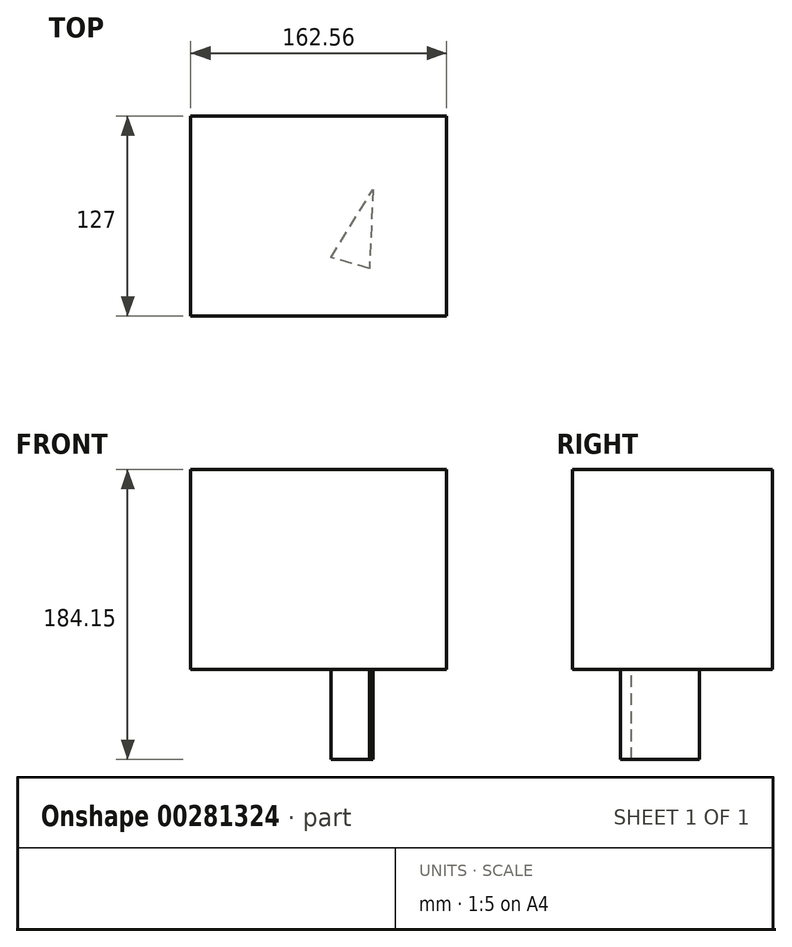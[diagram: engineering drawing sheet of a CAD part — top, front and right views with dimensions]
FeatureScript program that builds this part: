
annotation { "Feature Type Name" : "Feature", "Feature Type Description" : "" }
export const myFeature = defineFeature(function(context is Context, id is Id, definition is map)
    precondition{}
    {
        {
            var Q0;
            Q0=qCreatedBy(makeId("Front.planeOp"),FACE);
            var sketch = newSketch(context, id + "F0", { "sketchPlane" : qUnion([Q0])});
            skLineSegment(sketch, "E0.bottom", {"start": v(-127, 0) * mm, "end": v(0, 0) * mm});
            skLineSegment(sketch, "E0.top", {"start": v(-127, 127) * mm, "end": v(0, 127) * mm});
            skLineSegment(sketch, "E0.left", {"start": v(-127, 0) * mm, "end": v(-127, 127) * mm});
            skLineSegment(sketch, "E0.right", {"start": v(0, 0) * mm, "end": v(0, 127) * mm});
            skSolve(sketch);
        }
        {
            var Q0;
            Q0=qCreatedBy(makeId("Top.planeOp"),FACE);
            var sketch = newSketch(context, id + "F1", { "sketchPlane" : qUnion([Q0])});
            skLineSegment(sketch, "E1.bottom", {"start": v(0, 0) * mm, "end": v(0, 0) * mm});
            skLineSegment(sketch, "E1.top", {"start": v(0, -127) * mm, "end": v(0, -127) * mm});
            skLineSegment(sketch, "E1.left", {"start": v(0, 0) * mm, "end": v(0, -127) * mm});
            skLineSegment(sketch, "E1.right", {"start": v(0, 0) * mm, "end": v(0, -127) * mm});
            skLineSegment(sketch, "E2.left", {"start": v(0, -127) * mm, "end": v(0, 0) * mm});
            skLineSegment(sketch, "E2.right", {"start": v(0, -127) * mm, "end": v(0, 0) * mm});
            skLineSegment(sketch, "E3.bottom", {"start": v(0, -127) * mm, "end": v(-127, -127) * mm});
            skLineSegment(sketch, "E3.top", {"start": v(0, 0) * mm, "end": v(-127, 0) * mm});
            skLineSegment(sketch, "E3.right", {"start": v(-127, -127) * mm, "end": v(-127, 0) * mm});
            skSolve(sketch);
        }
        {
            var Q0;
            Q0=makeQuery(id+"F1.imprint","IMPRINT",FACE,{"disambiguationData":[TD([[makeQuery(id+"F1.imprint","IMPRINT",EDGE,{"derivedFrom":sQuery(id+"F1.wireOp",EDGE,"E3.bottom")}),-1.0]])]});
            extrude(context, id + "F2", {"entities" : qUnion([Q0]), "depth" : 127 * mm});
        }
        {
            var Q0;
            Q0=makeQuery(id+"F2.opExtrude","SWEPT_FACE",FACE,{"disambiguationData":[OSD([sQuery(id+"F1.wireOp",EDGE,"E3.right")])]});
            var sketch = newSketch(context, id + "F3", { "sketchPlane" : qUnion([Q0])});
            skSolve(sketch);
        }
        {
            var Q0;
            {var subQ0=sQuery(id+"F1.wireOp",EDGE,"E3.right");Q0=makeQuery(id+"F3.imprint","IMPRINT",FACE,{"disambiguationData":[TD([[makeQuery(id+"F3.imprint","IMPRINT",EDGE,{"derivedFrom":makeQuery(id+"F2.opExtrude","CAP_EDGE",EDGE,{"disambiguationData":[OSD([subQ0])],"isStart":true})}),-1.0]])]});}
            var sketch = newSketch(context, id + "F4", { "sketchPlane" : qUnion([Q0])});
            skCircle(sketch, "E4", {"center": v(63.3, 61.73) * mm, "radius": 31.75 * mm});
            skCircle(sketch, "E5", {"center": v(63.3, 61.73) * mm, "radius": 48.75 * mm});
            skSolve(sketch);
        }
        {
            var Q0;
            {var subQ0=sQuery(id+"F1.wireOp",EDGE,"E3.right");Q0=makeQuery(id+"F3.imprint","IMPRINT",FACE,{"disambiguationData":[TD([[makeQuery(id+"F3.imprint","IMPRINT",EDGE,{"derivedFrom":makeQuery(id+"F2.opExtrude","CAP_EDGE",EDGE,{"disambiguationData":[OSD([subQ0])],"isStart":true})}),-1.0]])]});}
            var sketch = newSketch(context, id + "F5", { "sketchPlane" : qUnion([Q0])});
            skSolve(sketch);
        }
        {
            var Q0;
            Q0=sQuery(id+"F4.wireOp",EDGE,"E4");
            var Q1;
            Q1=sQuery(id+"F4.wireOp",EDGE,"E5");
            extrude(context, id + "F6", {"bodyType" : ToolBodyType.SURFACE, "surfaceEntities" : qUnion([Q0, Q1]), "depth" : 127 * mm});
        }
        {
            var Q0;
            {var subQ0=sQuery(id+"F1.wireOp",EDGE,"E3.right");Q0=makeQuery(id+"F5.imprint","IMPRINT",FACE,{"disambiguationData":[TD([[makeQuery(id+"F5.imprint","IMPRINT",EDGE,{"derivedFrom":makeQuery(id+"F3.imprint","IMPRINT",EDGE,{"derivedFrom":makeQuery(id+"F2.opExtrude","CAP_EDGE",EDGE,{"disambiguationData":[OSD([subQ0])],"isStart":true})})}),-1.0]])]});}
            extrude(context, id + "F7", {"entities" : qUnion([Q0]), "operationType" : NewBodyOperationType.ADD, "depth" : 35.56 * mm});
        }
        {
            var Q0;
            {var subQ0=sQuery(id+"F1.wireOp",EDGE,"E3.right");Q0=makeQuery(id+"F7.boolean.opBoolean","MERGE",FACE,{"derivedFrom":[makeQuery(id+"F2.opExtrude","CAP_FACE",FACE,{"disambiguationData":[OSD([sQuery(id+"F1.wireOp",EDGE,"E3.bottom"),sQuery(id+"F1.wireOp",EDGE,"E3.top"),sQuery(id+"F1.wireOp",EDGE,"E2.left"),subQ0])],"isStart":true}),makeQuery(id+"F7.opExtrude","SWEPT_FACE",FACE,{"disambiguationData":[OSD([subQ0]),TDD([makeQuery(id+"F5.imprint","IMPRINT",EDGE,{"derivedFrom":makeQuery(id+"F3.imprint","IMPRINT",EDGE,{"derivedFrom":makeQuery(id+"F2.opExtrude","CAP_EDGE",EDGE,{"disambiguationData":[OSD([subQ0])],"isStart":true})})})])]})]});}
            var sketch = newSketch(context, id + "F8", { "sketchPlane" : qUnion([Q0])});
            skLineSegment(sketch, "E6", {"start": v(-49.1, 96.69) * mm, "end": v(-73.53, 89.75) * mm});
            skLineSegment(sketch, "E7", {"start": v(-73.53, 89.75) * mm, "end": v(-46.78, 46.56) * mm});
            skLineSegment(sketch, "E8", {"start": v(-46.78, 46.56) * mm, "end": v(-49.1, 96.69) * mm});
            skSolve(sketch);
        }
        {
            var Q0;
            Q0=makeQuery(id+"F8.imprint","IMPRINT",FACE,{"disambiguationData":[TD([[makeQuery(id+"F8.imprint","IMPRINT",EDGE,{"derivedFrom":sQuery(id+"F8.wireOp",EDGE,"E6")}),1.0]])]});
            var sketch = newSketch(context, id + "F9", { "sketchPlane" : qUnion([Q0])});
            skSolve(sketch);
        }
        {
            var Q0;
            Q0 = qSketchRegion(id + "F9", true);
            var Q1;
            Q1=makeQuery(id+"F8.imprint","IMPRINT",FACE,{"disambiguationData":[TD([[makeQuery(id+"F8.imprint","IMPRINT",EDGE,{"derivedFrom":sQuery(id+"F8.wireOp",EDGE,"E6")}),1.0]])]});
            extrude(context, id + "F10", {"entities" : qUnion([Q0, Q1]), "operationType" : NewBodyOperationType.ADD, "depth" : 57.15 * mm});
        }
        {
            var Q0;
            Q0=makeQuery(id+"F7.opExtrude","CAP_FACE",FACE,{"disambiguationData":[OSD([sQuery(id+"F1.wireOp",EDGE,"E3.bottom"),sQuery(id+"F1.wireOp",EDGE,"E3.top"),sQuery(id+"F1.wireOp",EDGE,"E3.right")])],"isStart":false});
            var sketch = newSketch(context, id + "F11", { "sketchPlane" : qUnion([Q0])});
            skSolve(sketch);
        }
        {
            var Q0;
            Q0=sQuery(id+"F4.wireOp",EDGE,"E5");
            var Q1;
            Q1=sQuery(id+"F4.wireOp",EDGE,"E4");
            extrude(context, id + "F12", {"bodyType" : ToolBodyType.SURFACE, "surfaceEntities" : qUnion([Q0, Q1]), "depth" : 50.8 * mm});
        }
        {
            var Q0;
            Q0=sQuery(id+"F4.wireOp",EDGE,"E4");
            var Q1;
            Q1=sQuery(id+"F4.wireOp",EDGE,"E5");
            extrude(context, id + "F13", {"bodyType" : ToolBodyType.SURFACE, "surfaceEntities" : qUnion([Q0, Q1]), "depth" : 233.68 * mm});
        }
    });
